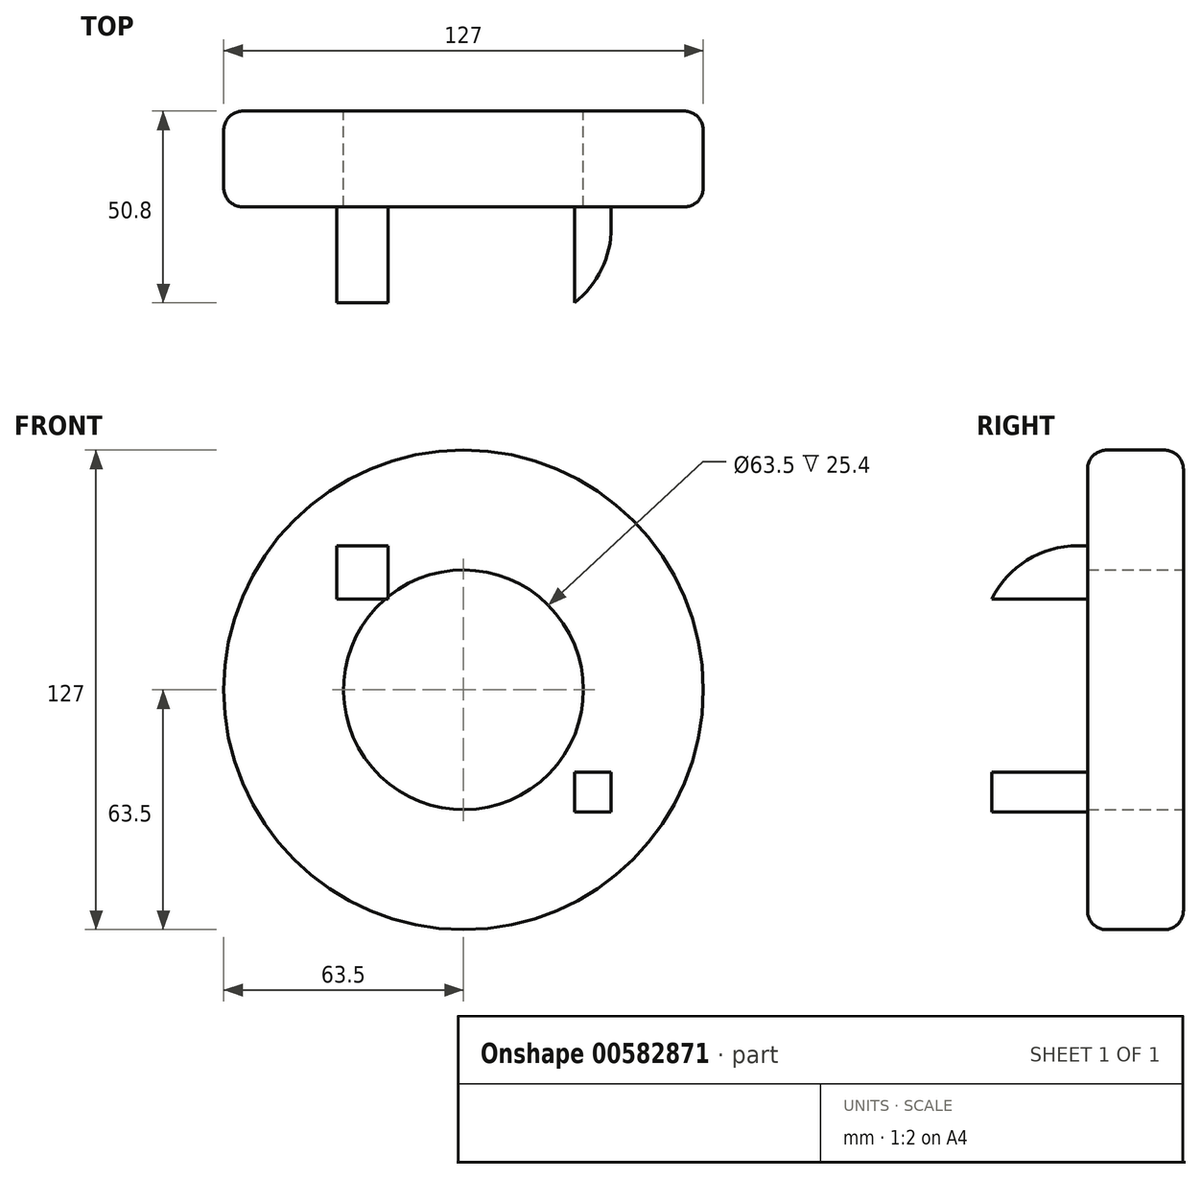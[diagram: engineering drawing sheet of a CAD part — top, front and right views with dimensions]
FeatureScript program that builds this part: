
annotation { "Feature Type Name" : "Feature", "Feature Type Description" : "" }
export const myFeature = defineFeature(function(context is Context, id is Id, definition is map)
    precondition{}
    {
        {
            var Q0;
            Q0=qCreatedBy(makeId("Front.planeOp"),FACE);
            var sketch = newSketch(context, id + "F0", { "sketchPlane" : qUnion([Q0])});
            skCircle(sketch, "E0", {"center": v(0, 0) * mm, "radius": 63.5 * mm});
            skCircle(sketch, "E1", {"center": v(0, 0) * mm, "radius": 31.75 * mm});
            skSolve(sketch);
        }
        {
            var Q0;
            Q0=makeQuery(id+"F0.imprint","IMPRINT",FACE,{"disambiguationData":[TD([[makeQuery(id+"F0.imprint","IMPRINT",EDGE,{"derivedFrom":sQuery(id+"F0.wireOp",EDGE,"E0")}),1.0]])]});
            extrude(context, id + "F1", {"entities" : qUnion([Q0]), "depth" : 25.4 * mm, "offsetDistance" : 25.4 * mm});
        }
        {
            var Q0;
            Q0=makeQuery(id+"F1.opExtrude","CAP_EDGE",EDGE,{"disambiguationData":[OSD([sQuery(id+"F0.wireOp",EDGE,"E0")])],"isStart":false});
            fillet(context, id + "F2", {"entities" : qUnion([Q0]), "radius" : 5.08 * mm, "tangentPropagation" : true, "allowEdgeOverflow" : false});
        }
        {
            var Q0;
            Q0=makeQuery(id+"F1.opExtrude","CAP_EDGE",EDGE,{"disambiguationData":[OSD([sQuery(id+"F0.wireOp",EDGE,"E0")])],"isStart":true});
            fillet(context, id + "F3", {"entities" : qUnion([Q0]), "radius" : 5.08 * mm, "tangentPropagation" : true, "allowEdgeOverflow" : false});
        }
        {
            var Q0;
            Q0=qCreatedBy(makeId("Front.planeOp"),FACE);
            var sketch = newSketch(context, id + "F4", { "sketchPlane" : qUnion([Q0])});
            skCircle(sketch, "E2", {"center": v(0, -51.83) * mm, "radius": 6.35 * mm});
            skCircle(sketch, "E3", {"center": v(0, 48.79) * mm, "radius": 6.35 * mm});
            skCircle(sketch, "E4", {"center": v(-47.36, 0) * mm, "radius": 6.35 * mm});
            skCircle(sketch, "E5", {"center": v(51.17, 0) * mm, "radius": 6.35 * mm});
            skSolve(sketch);
        }
        {
            var Q0;
            Q0=sQuery(id+"F4.wireOp",EDGE,"E3");
            var Q1;
            Q1=sQuery(id+"F4.wireOp",EDGE,"E4");
            var Q2;
            Q2=sQuery(id+"F4.wireOp",EDGE,"E2");
            var Q3;
            Q3=sQuery(id+"F4.wireOp",EDGE,"E5");
            extrude(context, id + "F5", {"bodyType" : ToolBodyType.SURFACE, "surfaceEntities" : qUnion([Q0, Q1, Q2, Q3]), "endBound" : BoundingType.THROUGH_ALL, "oppositeDirection" : true, "depth" : 25.4 * mm, "offsetDistance" : 25.4 * mm});
        }
        {
            var Q0;
            Q0=makeQuery(id+"F1.opExtrude","CAP_FACE",FACE,{"disambiguationData":[OSD([sQuery(id+"F0.wireOp",EDGE,"E0"),sQuery(id+"F0.wireOp",EDGE,"E1")])],"isStart":false});
            var sketch = newSketch(context, id + "F6", { "sketchPlane" : qUnion([Q0])});
            skLineSegment(sketch, "E6.bottom", {"start": v(39.14, -21.76) * mm, "end": v(29.36, -21.76) * mm});
            skLineSegment(sketch, "E6.top", {"start": v(39.14, -32.39) * mm, "end": v(29.36, -32.39) * mm});
            skLineSegment(sketch, "E6.left", {"start": v(39.14, -21.76) * mm, "end": v(39.14, -32.39) * mm});
            skLineSegment(sketch, "E6.right", {"start": v(29.36, -21.76) * mm, "end": v(29.36, -32.39) * mm});
            skPoint(sketch, "E6.middle", {"position": v(34.25, -27.07) * mm});
            skLineSegment(sketch, "E7.bottom", {"start": v(-19.98, 38.16) * mm, "end": v(-33.54, 38.16) * mm});
            skLineSegment(sketch, "E7.top", {"start": v(-19.98, 24.02) * mm, "end": v(-33.54, 24.02) * mm});
            skLineSegment(sketch, "E7.left", {"start": v(-19.98, 38.16) * mm, "end": v(-19.98, 24.02) * mm});
            skLineSegment(sketch, "E7.right", {"start": v(-33.54, 38.16) * mm, "end": v(-33.54, 24.02) * mm});
            skPoint(sketch, "E7.middle", {"position": v(-26.76, 31.1) * mm});
            skSolve(sketch);
        }
        {
            var Q0;
            Q0 = qSketchRegion(id + "F6", true);
            extrude(context, id + "F7", {"entities" : qUnion([Q0]), "operationType" : NewBodyOperationType.ADD, "depth" : 25.4 * mm, "offsetDistance" : 25.4 * mm});
        }
        {
            var Q0;
            Q0=makeQuery(id+"F7.opExtrude","CAP_EDGE",EDGE,{"disambiguationData":[OSD([sQuery(id+"F6.wireOp",EDGE,"E7.bottom")])],"isStart":false});
            fillet(context, id + "F8", {"entities" : qUnion([Q0]), "radius" : 25.4 * mm, "tangentPropagation" : true, "allowEdgeOverflow" : false});
        }
        {
            var Q0;
            Q0=makeQuery(id+"F7.opExtrude","CAP_EDGE",EDGE,{"disambiguationData":[OSD([sQuery(id+"F6.wireOp",EDGE,"E6.left")])],"isStart":false});
            fillet(context, id + "F9", {"entities" : qUnion([Q0]), "radius" : 25.4 * mm, "tangentPropagation" : true, "allowEdgeOverflow" : false});
        }
    });
